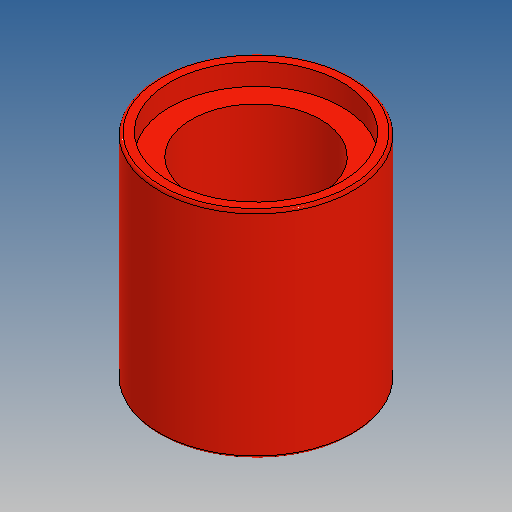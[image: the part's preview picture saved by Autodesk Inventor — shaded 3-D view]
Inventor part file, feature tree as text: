
AUTODESK INVENTOR PART (.ipt)
format: ipt  version: 2025 (Build 290162010, 162A)  size: 142,848 bytes
history: native  units: in
note: dims shown in document units (in); Inventor stores cm internally (conversion verified against a paired STEP export)
features: revolve x1, fillet x1, sketch x1
ambient origin geometry x8: Origin, YZ Plane, XZ Plane, XY Plane, X Axis, Y Axis, Z Axis, Center Point
bodies: Solid1 (feature_tree)
feature tree (3):
  revolve  "Revolution1"  [1 undecoded]
  fillet  "Fillet1"  Radius=0.252in
  sketch  "Sketch1"  dims[d0=0.189in d1=0.315in d2=0.252in d3=0.0315in d4=0.2835in d5=90.0deg d6=0.0039in d7=0.0in d8=0.0in]
note: 1 required parameter value undecoded (feature->parameter linkage not recoverable at this tier; creation-order binding heuristic only, values carry confidence <= 0.55)
